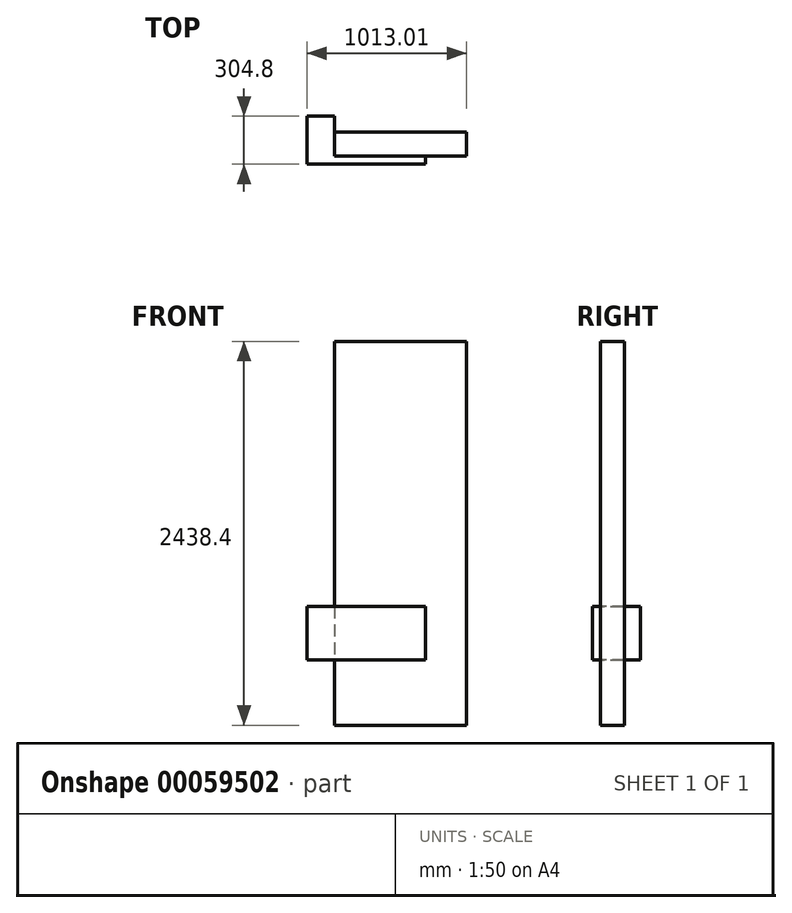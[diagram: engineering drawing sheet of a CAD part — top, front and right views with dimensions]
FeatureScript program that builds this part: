
annotation { "Feature Type Name" : "Feature", "Feature Type Description" : "" }
export const myFeature = defineFeature(function(context is Context, id is Id, definition is map)
    precondition{}
    {
        {
            var Q0;
            Q0=qCreatedBy(makeId("Front.planeOp"),FACE);
            var sketch = newSketch(context, id + "F0", { "sketchPlane" : qUnion([Q0])});
            skLineSegment(sketch, "E0.rect.bottom", {"start": v(419.1, 1219.2) * mm, "end": v(-419.1, 1219.2) * mm});
            skLineSegment(sketch, "E0.rect.top", {"start": v(419.1, -1219.2) * mm, "end": v(-419.1, -1219.2) * mm});
            skLineSegment(sketch, "E0.rect.left", {"start": v(419.1, 1219.2) * mm, "end": v(419.1, -1219.2) * mm});
            skLineSegment(sketch, "E0.rect.right", {"start": v(-419.1, 1219.2) * mm, "end": v(-419.1, -1219.2) * mm});
            skPoint(sketch, "E0.rect.middle", {"position": v(0, 0) * mm});
            skSolve(sketch);
        }
        {
            var Q0;
            Q0 = qSketchRegion(id + "F0", true);
            extrude(context, id + "F1", {"entities" : qUnion([Q0]), "depth" : 152.4 * mm});
        }
        {
            var Q0;
            Q0=makeQuery(id+"F1.opExtrude","CAP_FACE",FACE,{"disambiguationData":[OSD([sQuery(id+"F0.wireOp",EDGE,"E0.rect.bottom"),sQuery(id+"F0.wireOp",EDGE,"E0.rect.top"),sQuery(id+"F0.wireOp",EDGE,"E0.rect.left"),sQuery(id+"F0.wireOp",EDGE,"E0.rect.right")])],"isStart":false});
            var sketch = newSketch(context, id + "F2", { "sketchPlane" : qUnion([Q0])});
            skLineSegment(sketch, "E1.bottom", {"start": v(-593.91, -464.65) * mm, "end": v(158.11, -464.65) * mm});
            skLineSegment(sketch, "E1.top", {"start": v(-593.91, -804.56) * mm, "end": v(158.11, -804.56) * mm});
            skLineSegment(sketch, "E1.left", {"start": v(-593.91, -464.65) * mm, "end": v(-593.91, -804.56) * mm});
            skLineSegment(sketch, "E1.right", {"start": v(158.11, -464.65) * mm, "end": v(158.11, -804.56) * mm});
            skSolve(sketch);
        }
        {
            var Q0;
            Q0 = qSketchRegion(id + "F2", true);
            extrude(context, id + "F3", {"entities" : qUnion([Q0]), "operationType" : NewBodyOperationType.ADD, "depth" : 50.8 * mm});
        }
        {
            var Q0;
            Q0=makeQuery(id+"F3.opExtrude","CAP_FACE",FACE,{"disambiguationData":[OSD([sQuery(id+"F2.wireOp",EDGE,"E1.bottom"),sQuery(id+"F2.wireOp",EDGE,"E1.top"),sQuery(id+"F2.wireOp",EDGE,"E1.left"),sQuery(id+"F2.wireOp",EDGE,"E1.right")])],"isStart":true});
            var sketch = newSketch(context, id + "F4", { "sketchPlane" : qUnion([Q0])});
            skLineSegment(sketch, "E2.bottom", {"start": v(593.91, -464.65) * mm, "end": v(419.1, -464.65) * mm});
            skLineSegment(sketch, "E2.top", {"start": v(593.91, -804.56) * mm, "end": v(419.1, -804.56) * mm});
            skLineSegment(sketch, "E2.left", {"start": v(593.91, -464.65) * mm, "end": v(593.91, -804.56) * mm});
            skLineSegment(sketch, "E2.right", {"start": v(419.1, -464.65) * mm, "end": v(419.1, -804.56) * mm});
            skSolve(sketch);
        }
        {
            var Q0;
            Q0 = qSketchRegion(id + "F4", true);
            extrude(context, id + "F5", {"entities" : qUnion([Q0]), "operationType" : NewBodyOperationType.ADD, "depth" : 254 * mm});
        }
    });
